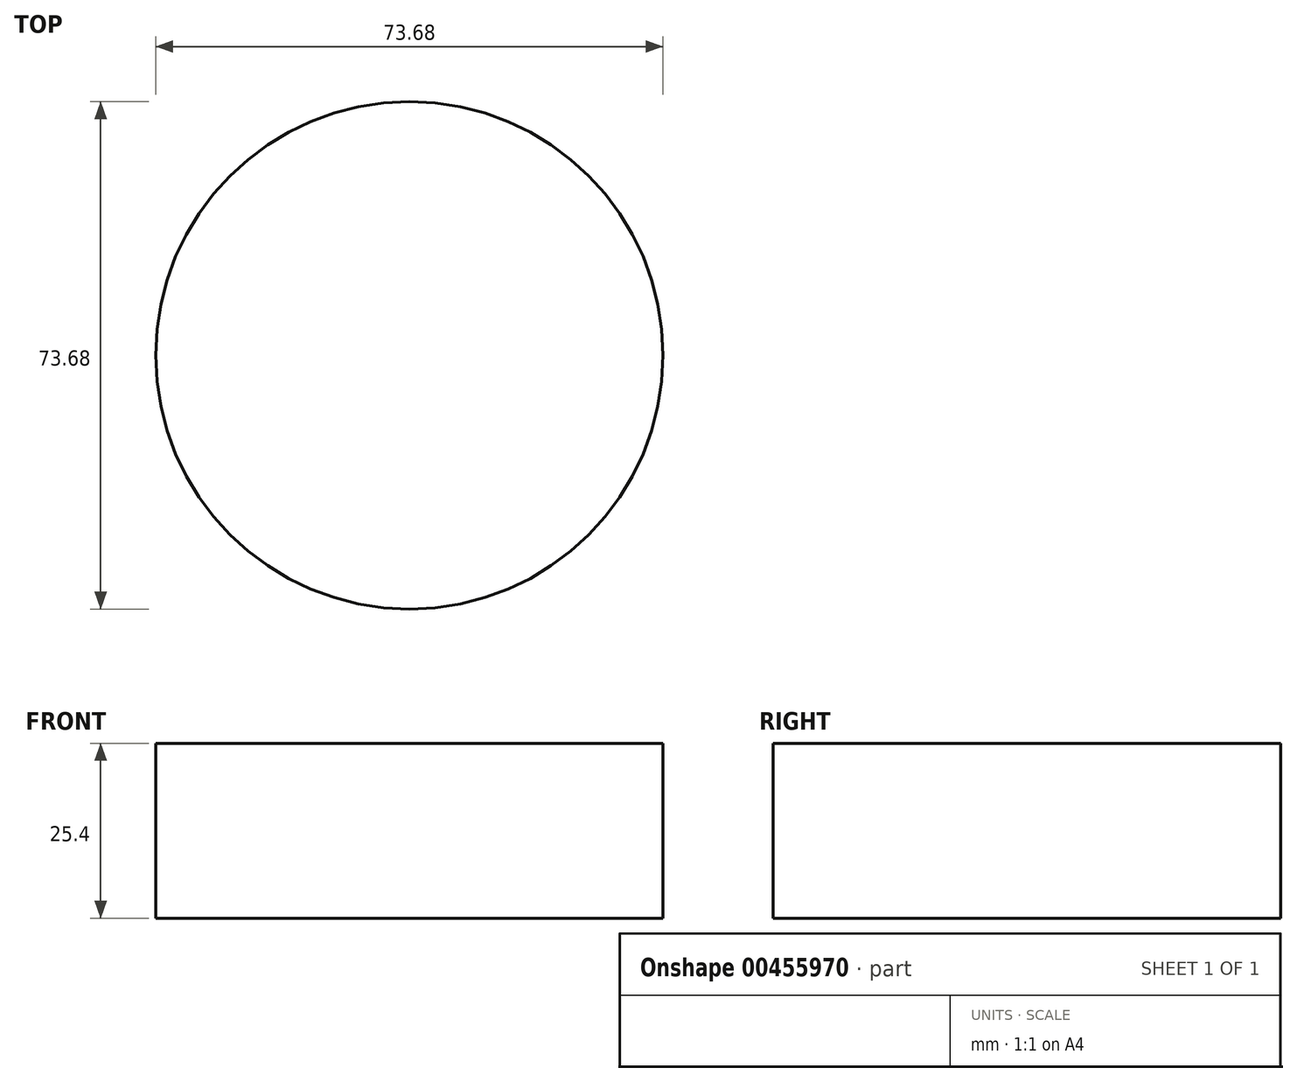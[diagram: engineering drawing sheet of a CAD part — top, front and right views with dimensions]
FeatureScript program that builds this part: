
annotation { "Feature Type Name" : "Feature", "Feature Type Description" : "" }
export const myFeature = defineFeature(function(context is Context, id is Id, definition is map)
    precondition{}
    {
        {
            var Q0;
            Q0=qCreatedBy(makeId("Top.planeOp"),FACE);
            var sketch = newSketch(context, id + "F0", { "sketchPlane" : qUnion([Q0])});
            skCircle(sketch, "E0", {"center": v(0, 0) * mm, "radius": 36.84 * mm});
            skSolve(sketch);
        }
        {
            var Q0;
            Q0 = qSketchRegion(id + "F0", true);
            extrude(context, id + "F1", {"entities" : qUnion([Q0]), "depth" : 25.4 * mm});
        }
    });
